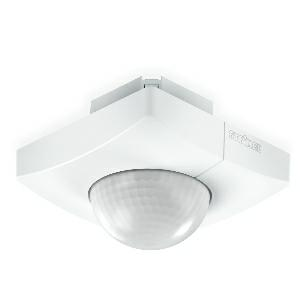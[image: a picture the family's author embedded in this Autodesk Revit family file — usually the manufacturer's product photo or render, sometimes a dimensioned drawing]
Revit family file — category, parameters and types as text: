
# Revit family: is_3360_058173
name_source: partatom
category: Elektroinstallationen
revit_build: Autodesk Revit 2016 (Build: 20190508_0715(x64)
units: mm (PartAtom-declared; Revit-internal decimal feet)

## family parameters
Basisbauteil = Fläche
Beim Laden mit Abzugskörper schneiden = Nein
Bemaßung runder Anschluss = Durchmesser verwenden
Beschriftungsausrichtung beibehalten = Nein
Gemeinsam genutzt = Nein
Raumberechnungspunkt = Nein
Teiletyp = Normal

## types (1)
- IS 3360
    Apparent Load = 0 VA
    Beschreibung = Type: Motion and Presence Detector; Dimensions (L x W x H): 78 x 94 x 94 mm; Power supply, detail: KNX bus; Sensor Technology: passive infrared; Application, place: Indoors; Application, room: production facilities, recreation room, changing room, function room / ancillary room, sports hall, reception / lobby, stairwell, WC / washroom, multi-storey / underground car park, warehouse, Indoors; Installation site: ceiling; Installation: Concealed wiring; Switching zones: 1416 switching zones; Electronic scalability: No; Mechanical scalability: No; Mounting height: 2,50 – 4,00 m; Optimum mounting height: 2,8 m; Detection angle: 360 °; Angle of aperture: 160 °; Sneak-by guard: Yes; Capability of masking out individual segments: Yes; Reach, radial: Ø 8 m (50 m²); Reach, tangential: Ø 40 m (1257 m²); Reach, presence: Ø 3 m (7 m²); Twilight setting TEACH: Yes; Twilight setting: 2 – 1000 lx; Time setting: 0 sec – 1092 min; Constant-lighting control: Yes; Basic light level function: Yes; KNX functions: Photo-cell controller, Basic light level function, Light level, HVAC output, Constant-lighting control, Light output 2x, Presence output, Day / night function; With bus coupling: Yes; Settings via: ETS software, Remote control, Bus, Smart Remote; IP-rating: IP20; Material: Plastic; Ambient temperature: -20 – 50 °C; Colour: white; Colour, RAL: 9010; Manufacturer's Warranty: 5 years; Version: KNX - concealed, sq. white; PU1, EAN: 4007841058173
    Height = 0 mm  [stored 0 ft]
    Hersteller = Steinel
    Length = 78 mm  [stored 0.255906 ft]
    Maximum range = 20.158 m
    ModVariant = Nein
    Modell = 058173
    Mounting Place = Ceiling
    Mounting Type = Recessed
    Number of Poles = 1
    OnlyDefault = Ja
    Power Factor = 1
    Product Name = IS 3360
    Product group = Presence detector
    ProductGroupID = 4
    Protection Class = Protection class
    Protection Degree = IP 20
    RlxData = <blob elided: 159017 chars, md5=c1ca9444>
    Sensor characteristics = Circular 300°-360°
    Sensor type = Passive (infrared)
    SensorDataFile = <blob elided: 6785 chars, md5=23016e95>
    Type of entry = Presence, Motion
    Typenbild = produkt1_058173.jpg
    Typenkommentare = Product without accessories
    URL = http://relux.com
    VarID = ---
    Voltage = 0 V
    Vorgabe-Ansicht = 1800 mm
    Weight = 0.00 kg
    Width = 94 mm  [stored 0.308399 ft]

note: [stored X ft] marks values corroborated as IEEE doubles in the binary element streams (Revit-internal decimal feet)

## geometry (parser evidence)
native form markers: Blend x4, Sweep x16
no freeform markers — native parametric forms only
